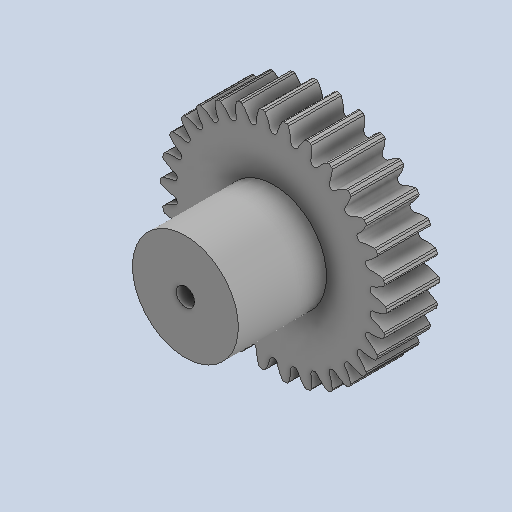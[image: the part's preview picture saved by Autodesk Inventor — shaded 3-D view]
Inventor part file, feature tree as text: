
AUTODESK INVENTOR PART (.ipt)
format: ipt  version: 2024 (Build 280153000, 153)  size: 752,640 bytes
history: native  units: mm
features: extrude x4, pattern_circular x2, fillet x1, sketch x1, other x1
ambient origin geometry x8: Origin, YZ Plane, XZ Plane, XY Plane, X Axis, Y Axis, Z Axis, Center Point
bodies: Solid1 (feature_tree)
feature tree (9):
  extrude  "Extrusion1"  TaperAngle=0.0deg  [1 undecoded]
  extrude  "Extrusion2"  Depth=300.0mm TaperAngle=360.0deg
  pattern_circular  "Circular Pattern1"  Count=3  [1 undecoded]
  extrude  "Extrusion3"  Depth=5.2mm
  fillet  "Fillet1"  Radius=25.0mm
  pattern_circular  "Circular Pattern2"  [2 undecoded]
  sketch  "Sketch2"  dims[d0=15.0mm d1=0.0mm d2=0.0mm d3=0.0mm d4=300.0mm d5=360.0deg d7=30.0mm d8=5.2mm d9=25.0mm d10=0.0mm d11=0.5mm d12=300.0mm d13=360.0deg d15=0.0mm d16=0.0mm d14=0.0mm]
  other  "Srf1"
  extrude  "ExtrusionSrf1"  Depth=300.0mm TaperAngle=360.0deg
note: 4 required parameter values undecoded (feature->parameter linkage not recoverable at this tier; creation-order binding heuristic only, values carry confidence <= 0.55)
